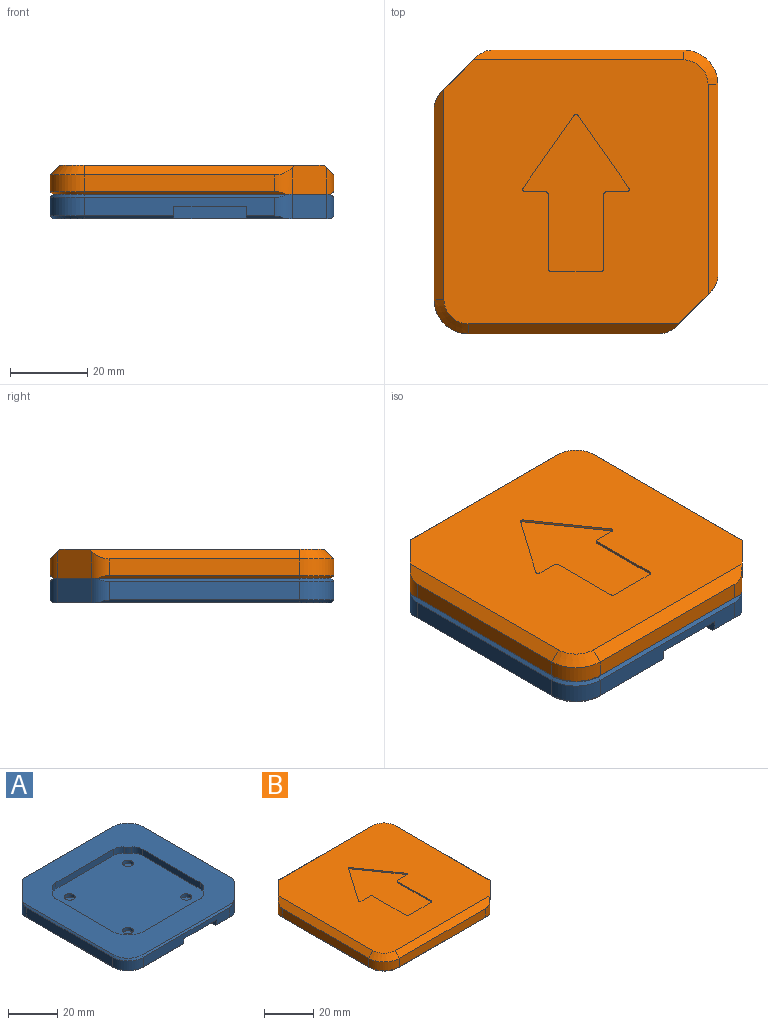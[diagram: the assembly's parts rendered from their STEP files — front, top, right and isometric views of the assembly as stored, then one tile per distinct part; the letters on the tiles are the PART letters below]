
ASSEMBLY  parts=2 mates=1
PART A: 66 faces, bbox 73.7x73.7x6.4 mm
  f0: plane 49.44x4.83mm, normal (0,1,0), area 193.2mm2, adj f8,f9,f14,f16,f21,f27,f29,f30
  f1: plane 72.14x72.14mm, normal (0,0,1), area 2674.4mm2, adj f6,f7,f19,f20,f21,f22,f36,f37
  f2: plane 49.44x4.83mm, normal (-1,0,0), area 238.6mm2, adj f13,f18,f22,f65
  f3: plane 72.14x72.14mm, normal (0,0,-1), area 4730mm2, adj f4,f5,f8,f9,f10,f15,f16,f17
  f4: plane 52.46x0.76mm, normal (0.71,0,-0.71), area 55.5mm2, adj f3,f12,f15,f63
  f5: plane 10.42x0.76mm, normal (0,-0.71,-0.71), area 10.2mm2, adj f3,f11,f25,f62
  f6: plane 52.46x0.76mm, normal (0.71,0,0.71), area 55.5mm2, adj f1,f12,f19,f63
  f7: plane 52.46x0.76mm, normal (0,-0.71,0.71), area 55.5mm2, adj f1,f11,f20,f62
  f8: plane 10.42x0.76mm, normal (0,0.71,-0.71), area 10.2mm2, adj f0,f3,f31,f64
  f9: plane 9.4x0.76mm, normal (0,0.71,-0.71), area 10.1mm2, adj f0,f3,f29,f32
  f10: plane 23.24x0.76mm, normal (0,-0.71,-0.71), area 25mm2, adj f3,f11,f17,f23
  f11: plane 49.44x4.83mm, normal (0,-1,0), area 193.2mm2, adj f5,f7,f10,f13,f23,f25,f26,f62
  f12: plane 49.44x4.83mm, normal (1,0,0), area 238.6mm2, adj f4,f6,f14,f63
  f13: cylinder r=8.89mm len=8.89mm, axis (0,0,-1), area 67.4mm2, adj f2,f11,f17,f20
  f14: cylinder r=8.89mm len=8.89mm, axis (0,0,-1), area 67.4mm2, adj f0,f12,f15,f19
  f15: cone r=8.13mm half-angle=45deg, axis (0,0,1), area 14.4mm2, adj f3,f4,f14,f16
  f16: plane 13.84x0.76mm, normal (0,0.71,-0.71), area 14.9mm2, adj f0,f3,f15,f27
  f17: cone r=8.13mm half-angle=45deg, axis (0,0,1), area 14.4mm2, adj f3,f10,f13,f18
  f18: plane 52.46x0.76mm, normal (-0.71,0,-0.71), area 55.5mm2, adj f2,f3,f17,f65
  f19: cone r=8.13mm half-angle=45deg, axis (0,0,-1), area 14.4mm2, adj f1,f6,f14,f21
  f20: cone r=8.13mm half-angle=45deg, axis (0,0,-1), area 14.4mm2, adj f1,f7,f13,f22
  f21: plane 52.46x0.76mm, normal (0,0.71,0.71), area 55.5mm2, adj f0,f1,f19,f64
  f22: plane 52.46x0.76mm, normal (-0.71,0,0.71), area 55.5mm2, adj f1,f2,f20,f65
  f23: plane 9.4x3.18mm, normal (1,0,0), area 29.5mm2, adj f3,f10,f11,f24,f26
  f24: plane 18.8x3.18mm, normal (0,-1,0), area 59.7mm2, adj f3,f23,f25,f26
  f25: plane 9.4x3.18mm, normal (-1,0,0), area 29.5mm2, adj f3,f5,f11,f24,f26
  f26: plane 18.8x9.4mm, normal (0,0,-1), area 176.6mm2, adj f11,f23,f24,f25
  f27: plane 9.14x3.18mm, normal (-1,0,0), area 28.7mm2, adj f0,f3,f16,f28,f30
  f28: plane 9.4x3.18mm, normal (0,1,0), area 29.8mm2, adj f3,f27,f29,f30
  f29: plane 9.14x3.18mm, normal (1,0,0), area 28.7mm2, adj f0,f3,f9,f28,f30
  f30: plane 9.4x9.14mm, normal (0,0,-1), area 85.9mm2, adj f0,f27,f28,f29
  f31: plane 9.14x3.18mm, normal (1,0,0), area 28.7mm2, adj f0,f3,f8,f33,f34
  f32: plane 9.14x3.18mm, normal (-1,0,0), area 28.7mm2, adj f0,f3,f9,f33,f34
  f33: plane 9.4x3.18mm, normal (0,1,0), area 29.8mm2, adj f3,f31,f32,f34
  f34: plane 9.4x9.14mm, normal (0,0,-1), area 85.9mm2, adj f0,f31,f32,f33
  f35: plane 49.53x49.53mm, normal (0,0,1), area 2311.9mm2, adj f36,f37,f38,f39,f40,f41,f42,f43
  f36: plane 33.34x3.18mm, normal (0,-1,0), area 105.9mm2, adj f1,f35,f44,f45
  f37: cylinder r=8.89mm len=3.18mm, axis (0,0,1), area 8.6mm2, adj f1,f35,f45,f46
  f38: plane 33.34x3.18mm, normal (1,0,0), area 105.9mm2, adj f1,f35,f46,f47
  f39: cylinder r=8.89mm len=3.18mm, axis (0,0,1), area 8.6mm2, adj f1,f35,f47,f48
  f40: plane 33.34x3.18mm, normal (0,1,0), area 105.9mm2, adj f1,f35,f48,f49
  f41: cylinder r=8.89mm len=3.18mm, axis (0,0,1), area 8.6mm2, adj f1,f35,f44,f50
  f42: cylinder r=8.89mm len=3.18mm, axis (0,0,1), area 8.6mm2, adj f1,f35,f49,f51
  f43: plane 33.34x3.18mm, normal (-1,0,0), area 105.9mm2, adj f1,f35,f50,f51
  f44: cylinder r=5.08mm len=4.1mm, axis (0,0,1), area 15.1mm2, adj f1,f35,f36,f41
  f45: cylinder r=5.08mm len=4.1mm, axis (0,0,1), area 15.1mm2, adj f1,f35,f36,f37
  f46: cylinder r=5.08mm len=4.1mm, axis (0,0,1), area 15.1mm2, adj f1,f35,f37,f38
  f47: cylinder r=5.08mm len=4.1mm, axis (0,0,1), area 15.1mm2, adj f1,f35,f38,f39
  f48: cylinder r=5.08mm len=4.1mm, axis (0,0,1), area 15.1mm2, adj f1,f35,f39,f40
  f49: cylinder r=5.08mm len=4.1mm, axis (0,0,1), area 15.1mm2, adj f1,f35,f40,f42
  f50: cylinder r=5.08mm len=4.1mm, axis (0,0,1), area 15.1mm2, adj f1,f35,f41,f43
  f51: cylinder r=5.08mm len=4.1mm, axis (0,0,1), area 15.1mm2, adj f1,f35,f42,f43
  f52: plane 4.5x4.5mm, normal (0,0,1), area 15.9mm2, adj f53
  f53: cylinder r=2.25mm len=4.5mm, axis (0,0,1), area 22.4mm2, adj f35,f52
  f54: plane 4.5x4.5mm, normal (0,0,1), area 15.9mm2, adj f55
  f55: cylinder r=2.25mm len=4.5mm, axis (0,0,1), area 22.4mm2, adj f35,f54
  f56: plane 4.5x4.5mm, normal (0,0,1), area 15.9mm2, adj f57
  f57: cylinder r=2.25mm len=4.5mm, axis (0,0,1), area 22.4mm2, adj f35,f56
  f58: plane 4.5x4.5mm, normal (0,0,1), area 15.9mm2, adj f59
  f59: cylinder r=2.25mm len=4.5mm, axis (0,0,1), area 22.4mm2, adj f35,f58
  f60: plane 8.98x8.98mm, normal (-0.71,0.71,0), area 80.6mm2, adj f1,f3,f64,f65
  f61: plane 8.98x8.98mm, normal (0.71,-0.71,0), area 80.6mm2, adj f1,f3,f62,f63
  f62: cylinder r=6.35mm len=6.35mm, axis (0,0,-1), area 28.5mm2, adj f1,f3,f5,f7,f11,f61
  f63: cylinder r=6.35mm len=6.35mm, axis (0,0,1), area 28.5mm2, adj f1,f3,f4,f6,f12,f61
  f64: cylinder r=6.35mm len=6.35mm, axis (0,0,-1), area 28.5mm2, adj f0,f1,f3,f8,f21,f60
  f65: cylinder r=6.35mm len=6.35mm, axis (0,0,1), area 28.5mm2, adj f1,f2,f3,f18,f22,f60
PART B: 41 faces, bbox 73.7x73.7x7.6 mm
  f0: plane 68.58x68.58mm, normal (0,0,1), area 4032.3mm2, adj f8,f9,f10,f11,f18,f19,f20,f21
  f1: plane 49.44x4.32mm, normal (0,1,0), area 213.5mm2, adj f5,f11,f15,f40
  f2: plane 49.44x4.32mm, normal (-1,0,0), area 213.5mm2, adj f7,f9,f14,f39
  f3: plane 72.14x72.14mm, normal (0,0,-1), area 5049.8mm2, adj f4,f5,f6,f7,f16,f17,f35,f36
  f4: plane 52.46x0.76mm, normal (0.71,0,-0.71), area 55.5mm2, adj f3,f13,f16,f38
  f5: plane 52.46x0.76mm, normal (0,0.71,-0.71), area 55.5mm2, adj f1,f3,f16,f40
  f6: plane 52.46x0.76mm, normal (0,-0.71,-0.71), area 55.5mm2, adj f3,f12,f17,f37
  f7: plane 52.46x0.76mm, normal (-0.71,0,-0.71), area 55.5mm2, adj f2,f3,f17,f39
  f8: plane 54.61x2.54mm, normal (0,-0.71,0.71), area 190.4mm2, adj f0,f12,f18,f36,f37
  f9: plane 54.61x2.54mm, normal (-0.71,0,0.71), area 190.4mm2, adj f0,f2,f18,f35,f39
  f10: plane 54.61x2.54mm, normal (0.71,0,0.71), area 190.4mm2, adj f0,f13,f19,f36,f38
  f11: plane 54.61x2.54mm, normal (0,0.71,0.71), area 190.4mm2, adj f0,f1,f19,f35,f40
  f12: plane 49.44x4.32mm, normal (0,-1,0), area 213.5mm2, adj f6,f8,f14,f37
  f13: plane 49.44x4.32mm, normal (1,0,0), area 213.5mm2, adj f4,f10,f15,f38
  f14: cylinder r=8.89mm len=8.89mm, axis (0,0,-1), area 60.3mm2, adj f2,f12,f17,f18
  f15: cylinder r=8.89mm len=8.89mm, axis (0,0,-1), area 60.3mm2, adj f1,f13,f16,f19
  f16: cone r=8.13mm half-angle=45deg, axis (0,0,1), area 14.4mm2, adj f3,f4,f5,f15
  f17: cone r=8.13mm half-angle=45deg, axis (0,0,1), area 14.4mm2, adj f3,f6,f7,f14
  f18: cone r=6.35mm half-angle=45deg, axis (0,0,-1), area 43mm2, adj f0,f8,f9,f14
  f19: cone r=6.35mm half-angle=45deg, axis (0,0,-1), area 43mm2, adj f0,f10,f11,f15
  f20: plane 5.37x0.6mm, normal (0,1,0), area 3.2mm2, adj f0,f27,f28,f34
  f21: plane 19.37x0.6mm, normal (1,0,0), area 11.6mm2, adj f0,f27,f28,f29
  f22: plane 13.18x0.6mm, normal (0,1,0), area 7.9mm2, adj f0,f27,f29,f30
  f23: plane 19.37x0.6mm, normal (-1,0,0), area 11.6mm2, adj f0,f27,f30,f31
  f24: plane 5.37x0.6mm, normal (0,1,0), area 3.2mm2, adj f0,f27,f31,f32
  f25: plane 18.9x13.23mm, normal (-0.82,-0.57,0), area 13.8mm2, adj f0,f27,f32,f33
  f26: plane 18.9x13.23mm, normal (0.82,-0.57,0), area 13.8mm2, adj f0,f27,f33,f34
  f27: plane 40.8x27.73mm, normal (0,0,1), area 595.6mm2, adj f20,f21,f22,f23,f24,f25,f26,f28
  f28: cylinder r=0.64mm len=0.64mm, axis (0,0,1), area 0.6mm2, adj f0,f20,f21,f27
  f29: cylinder r=0.64mm len=0.64mm, axis (0,0,-1), area 0.6mm2, adj f0,f21,f22,f27
  f30: cylinder r=0.64mm len=0.64mm, axis (0,0,-1), area 0.6mm2, adj f0,f22,f23,f27
  f31: cylinder r=0.64mm len=0.64mm, axis (0,0,1), area 0.6mm2, adj f0,f23,f24,f27
  f32: cylinder r=0.64mm len=1mm, axis (0,0,-1), area 0.8mm2, adj f0,f24,f25,f27
  f33: cylinder r=0.64mm len=1.04mm, axis (0,0,-1), area 0.7mm2, adj f0,f25,f26,f27
  f34: cylinder r=0.64mm len=1mm, axis (0,0,-1), area 0.8mm2, adj f0,f20,f26,f27
  f35: plane 8.98x8.98mm, normal (-0.71,0.71,0), area 96.1mm2, adj f0,f3,f9,f11,f39,f40
  f36: plane 8.98x8.98mm, normal (0.71,-0.71,0), area 96.1mm2, adj f0,f3,f8,f10,f37,f38
  f37: cylinder r=6.35mm len=6.94mm, axis (0,0,-1), area 26.9mm2, adj f3,f6,f8,f12,f36
  f38: cylinder r=6.35mm len=6.94mm, axis (0,0,1), area 26.9mm2, adj f3,f4,f10,f13,f36
  f39: cylinder r=6.35mm len=6.94mm, axis (0,0,-1), area 26.9mm2, adj f2,f3,f7,f9,f35
  f40: cylinder r=6.35mm len=6.94mm, axis (0,0,1), area 26.9mm2, adj f1,f3,f5,f11,f35
PLACE A t=(-36.68,25.51,-23.3)mm fixed
PLACE B t=(-36.68,25.51,-16.95)mm
MATE planar B.f3 <-> A.f1  axis (0,0,-1) through (0.15,-11.32,-16.95)mm
